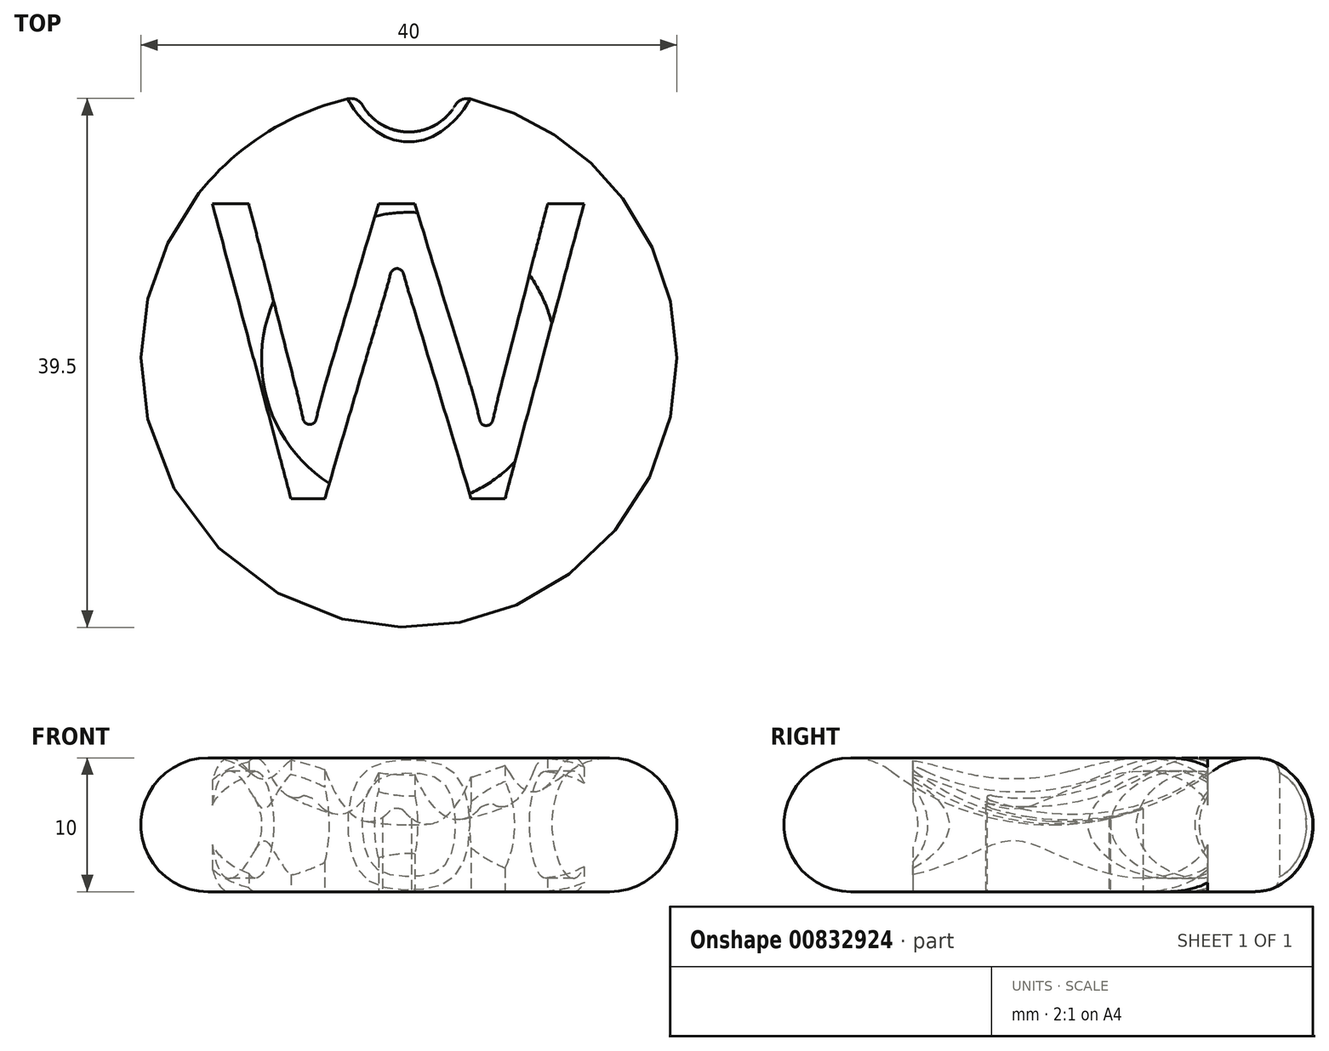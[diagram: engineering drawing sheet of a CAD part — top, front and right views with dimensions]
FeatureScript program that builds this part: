
annotation { "Feature Type Name" : "Feature", "Feature Type Description" : "" }
export const myFeature = defineFeature(function(context is Context, id is Id, definition is map)
    precondition{}
    {
        {
            var Q0;
            Q0=qCreatedBy(makeId("Front.planeOp"),FACE);
            var sketch = newSketch(context, id + "F0", { "sketchPlane" : qUnion([Q0])});
            skLineSegment(sketch, "E0", {"start": v(-15, 0) * mm, "end": v(0, 0) * mm});
            skLineSegment(sketch, "E1", {"start": v(0, 0) * mm, "end": v(0, 5) * mm});
            skArc(sketch, "E2", {"start": v(-12, 9) * mm, "mid": v(-19.74, 6.58) * mm, "end": v(-15, 0) * mm});
            skArc(sketch, "E3", {"start": v(-12, 9) * mm, "mid": v(-6.32, 6.03) * mm, "end": v(0, 5) * mm});
            skLineSegment(sketch, "E4", {"start": v(0, 5) * mm, "end": v(-108.23, 5) * mm, "construction": true});
            skCircle(sketch, "E5", {"center": v(-15, 5) * mm, "radius": 4 * mm});
            skSolve(sketch);
        }
        {
            var Q0;
            Q0=makeQuery(id+"F0.imprint","IMPRINT",FACE,{"disambiguationData":[TD([[makeQuery(id+"F0.imprint","IMPRINT",EDGE,{"derivedFrom":sQuery(id+"F0.wireOp",EDGE,"E0")}),1.0]])]});
            var Q1;
            Q1=sQuery(id+"F0.wireOp",EDGE,"E1");
            revolve(context, id + "F1", {"surfaceOperationType" : NewSurfaceOperationType.NEW, "entities" : qUnion([Q0]), "axis" : qUnion([Q1]), "revolveType" : RevolveType.FULL});
        }
        {
            var Q0;
            Q0=sQuery(id+"F0.wireOp",VERTEX,"E0.start");
            var Q1;
            Q1=sQuery(id+"F0.wireOp",EDGE,"E1");
            cPlane(context, id + "F2", {"entities" : qUnion([Q0, Q1]), "cplaneType" : CPlaneType.LINE_POINT, "offset" : 25 * mm, "width" : 150 * mm, "height" : 150 * mm});
        }
        {
            var Q0;
            Q0=qCreatedBy(id+"F2.planeOp",FACE);
            var sketch = newSketch(context, id + "F3", { "sketchPlane" : qUnion([Q0])});
            skText(sketch, "E6", { "text": "W", "fontName": "OpenSans-Regular.ttf"});
            const initialGuessF3  = {"E6": [-0.01507, -0.01039, 1, 0, 0.02221]};
            skSetInitialGuess(sketch, initialGuessF3);
            skSolve(sketch);
        }
        {
            var Q0;
            Q0 = qSketchRegion(id + "F3", true);
            extrude(context, id + "F4", {"entities" : qUnion([Q0]), "operationType" : NewBodyOperationType.REMOVE, "endBound" : BoundingType.THROUGH_ALL, "depth" : 25 * mm, "offsetDistance" : 25 * mm});
        }
        {
            var Q0;
            Q0=makeQuery(id+"F0.imprint","IMPRINT",FACE,{"disambiguationData":[TD([[makeQuery(id+"F0.imprint","IMPRINT",EDGE,{"derivedFrom":sQuery(id+"F0.wireOp",EDGE,"E5")}),1.0]])]});
            var Q1;
            Q1=sQuery(id+"F0.wireOp",EDGE,"E1");
            revolve(context, id + "F5", {"operationType" : NewBodyOperationType.ADD, "surfaceOperationType" : NewSurfaceOperationType.NEW, "entities" : qUnion([Q0]), "axis" : qUnion([Q1]), "revolveType" : RevolveType.FULL});
        }
        {
            var Q0;
            Q0=qCreatedBy(makeId("Top.planeOp"),FACE);
            var sketch = newSketch(context, id + "F6", { "sketchPlane" : qUnion([Q0])});
            skCircle(sketch, "E7", {"center": v(0, 21) * mm, "radius": 4 * mm});
            skSolve(sketch);
        }
        {
            var Q0;
            Q0=makeQuery(id+"F6.imprint","IMPRINT",FACE,{"disambiguationData":[TD([[makeQuery(id+"F6.imprint","IMPRINT",EDGE,{"derivedFrom":sQuery(id+"F6.wireOp",EDGE,"E7")}),1.0]])]});
            extrude(context, id + "F7", {"entities" : qUnion([Q0]), "operationType" : NewBodyOperationType.REMOVE, "endBound" : BoundingType.THROUGH_ALL, "depth" : 25 * mm, "offsetDistance" : 25 * mm});
        }
        {
            var Q0;
            Q0=makeQuery(id+"F7.boolean.opBoolean","INTERSECT",EDGE,{"derivedFrom":[makeQuery(id+"F1.opRevolve","SWEPT_FACE",FACE,{"disambiguationData":[OSD([sQuery(id+"F0.wireOp",EDGE,"E2")])]}),makeQuery(id+"F7.opExtrude","SWEPT_FACE",FACE,{"disambiguationData":[OSD([sQuery(id+"F6.wireOp",EDGE,"E7")])]})]});
            fillet(context, id + "F8", {"entities" : qUnion([Q0]), "radius" : 1 * mm, "tangentPropagation" : true, "allowEdgeOverflow" : false});
        }
        {
            var Q0;
            Q0=makeQuery(id+"F4.boolean.opBoolean","COPY",EDGE,{"derivedFrom":makeQuery(id+"F4.opExtrude","SWEPT_EDGE",EDGE,{"disambiguationData":[OSD([sQuery(id+"F3.wireOp",EDGE,"E6.sketch_text.stroke-10"),sQuery(id+"F3.wireOp",EDGE,"E6.sketch_text.stroke-11")])]})});
            var Q1;
            Q1=makeQuery(id+"F4.boolean.opBoolean","COPY",EDGE,{"derivedFrom":makeQuery(id+"F4.opExtrude","SWEPT_EDGE",EDGE,{"disambiguationData":[OSD([sQuery(id+"F3.wireOp",EDGE,"E6.sketch_text.stroke-15"),sQuery(id+"F3.wireOp",EDGE,"E6.sketch_text.stroke-16")])]})});
            var Q2;
            Q2=makeQuery(id+"F4.boolean.opBoolean","COPY",EDGE,{"derivedFrom":makeQuery(id+"F4.opExtrude","SWEPT_EDGE",EDGE,{"disambiguationData":[OSD([sQuery(id+"F3.wireOp",EDGE,"E6.sketch_text.stroke-3"),sQuery(id+"F3.wireOp",EDGE,"E6.sketch_text.stroke-4")])]})});
            fillet(context, id + "F9", {"entities" : qUnion([Q0, Q1, Q2]), "radius" : 0.5 * mm, "tangentPropagation" : true, "allowEdgeOverflow" : false});
        }
    });
